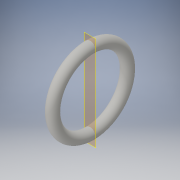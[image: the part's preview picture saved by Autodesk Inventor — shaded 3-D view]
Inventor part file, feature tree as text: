
AUTODESK INVENTOR PART (.ipt)
format: ipt  version: 2016 (Build 200138000, 138)  size: 133,120 bytes
history: native  units: in
note: dims shown in document units (in); Inventor stores cm internally (conversion verified against a paired STEP export)
features: sketch x4, sweep x1
ambient origin geometry x8: Origin, YZ Plane, XZ Plane, XY Plane, X Axis, Y Axis, Z Axis, Center Point
bodies: Solid1 (feature_tree)
feature tree (5):
  sketch  "Sketch1"  dims[d0=0.217in d2=1.512in]
  sketch  "Sketch2"  dims[d3=0.0in d4=0.0in]
  sketch  "Sketch3"
  sweep  "Sweep1"
  sketch  "Sketch4"
